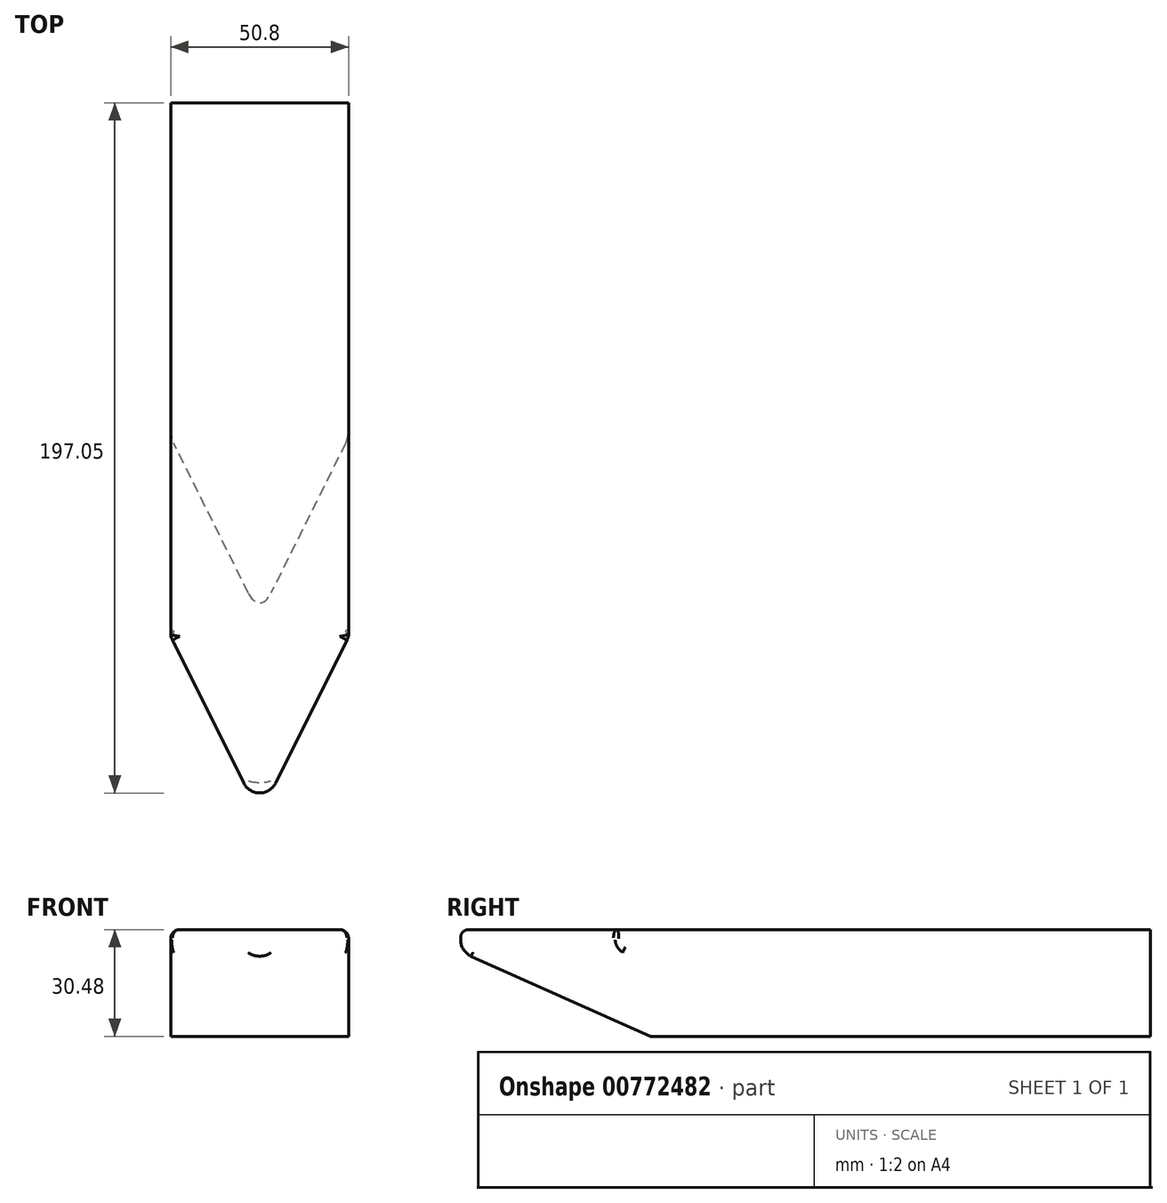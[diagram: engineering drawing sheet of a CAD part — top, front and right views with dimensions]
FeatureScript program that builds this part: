
annotation { "Feature Type Name" : "Feature", "Feature Type Description" : "" }
export const myFeature = defineFeature(function(context is Context, id is Id, definition is map)
    precondition{}
    {
        {
            var Q0;
            Q0=qCreatedBy(makeId("Top.planeOp"),FACE);
            var sketch = newSketch(context, id + "F0", { "sketchPlane" : qUnion([Q0])});
            skLineSegment(sketch, "E0.bottom", {"start": v(-25.4, 76.2) * mm, "end": v(25.4, 76.2) * mm});
            skLineSegment(sketch, "E0.top", {"start": v(-25.4, -76.2) * mm, "end": v(25.4, -76.2) * mm});
            skLineSegment(sketch, "E0.left", {"start": v(-25.4, 76.2) * mm, "end": v(-25.4, -76.2) * mm});
            skLineSegment(sketch, "E0.right", {"start": v(25.4, 76.2) * mm, "end": v(25.4, -76.2) * mm});
            skPoint(sketch, "E0.middle", {"position": v(0, 0) * mm});
            skLineSegment(sketch, "E1", {"start": v(-25.4, -76.2) * mm, "end": v(0, -127.15) * mm});
            skLineSegment(sketch, "E2", {"start": v(25.4, -76.2) * mm, "end": v(0, -127.15) * mm});
            skSolve(sketch);
        }
        {
            var Q0;
            Q0=makeQuery(id+"F0.imprint","IMPRINT",FACE,{"disambiguationData":[TD([[makeQuery(id+"F0.imprint","IMPRINT",EDGE,{"derivedFrom":sQuery(id+"F0.wireOp",EDGE,"E0.bottom")}),-1.0]])]});
            var Q1;
            Q1=makeQuery(id+"F0.imprint","IMPRINT",FACE,{"disambiguationData":[TD([[makeQuery(id+"F0.imprint","IMPRINT",EDGE,{"derivedFrom":sQuery(id+"F0.wireOp",EDGE,"E0.top")}),-1.0]])]});
            extrude(context, id + "F1", {"entities" : qUnion([Q0, Q1]), "depth" : 30.48 * mm, "offsetDistance" : 25.4 * mm});
        }
        {
            var Q0;
            Q0=makeQuery(id+"F1.opExtrude","CAP_EDGE",EDGE,{"disambiguationData":[OSD([sQuery(id+"F0.wireOp",EDGE,"E2")])],"isStart":true});
            var Q1;
            Q1=makeQuery(id+"F1.opExtrude","CAP_EDGE",EDGE,{"disambiguationData":[OSD([sQuery(id+"F0.wireOp",EDGE,"E1")])],"isStart":true});
            chamfer(context, id + "F2", {"entities" : qUnion([Q0, Q1]), "width" : 25.4 * mm, "tangentPropagation" : true});
        }
        {
            var Q0;
            {var subQ0=sQuery(id+"F0.wireOp",EDGE,"E2");Q0=makeQuery(id+"F2.opChamfer","BLEND_EDGE",EDGE,{"blendedFrom":[makeQuery(id+"F1.opExtrude","CAP_EDGE",EDGE,{"disambiguationData":[OSD([subQ0])],"isStart":true}),makeQuery(id+"F1.opExtrude","SWEPT_FACE",FACE,{"disambiguationData":[OSD([subQ0])]})],"blendedInto":[makeQuery(id+"F1.opExtrude","SWEPT_FACE",FACE,{"disambiguationData":[OSD([subQ0])]})]});}
            var Q1;
            {var subQ0=sQuery(id+"F0.wireOp",EDGE,"E1");Q1=makeQuery(id+"F2.opChamfer","BLEND_EDGE",EDGE,{"blendedFrom":[makeQuery(id+"F1.opExtrude","CAP_EDGE",EDGE,{"disambiguationData":[OSD([subQ0])],"isStart":true}),makeQuery(id+"F1.opExtrude","SWEPT_FACE",FACE,{"disambiguationData":[OSD([subQ0])]})],"blendedInto":[makeQuery(id+"F1.opExtrude","SWEPT_FACE",FACE,{"disambiguationData":[OSD([subQ0])]})]});}
            fillet(context, id + "F3", {"entities" : qUnion([Q0, Q1]), "radius" : 5.08 * mm, "tangentPropagation" : true, "allowEdgeOverflow" : false});
        }
        {
            var Q0;
            Q0=makeQuery(id+"F2.opChamfer","BLEND_EDGE",EDGE,{"blendedFrom":[makeQuery(id+"F1.opExtrude","CAP_EDGE",EDGE,{"disambiguationData":[OSD([sQuery(id+"F0.wireOp",EDGE,"E1")])],"isStart":true}),makeQuery(id+"F1.opExtrude","CAP_EDGE",EDGE,{"disambiguationData":[OSD([sQuery(id+"F0.wireOp",EDGE,"E2")])],"isStart":true})],"blendedInto":[]});
            fillet(context, id + "F4", {"entities" : qUnion([Q0]), "radius" : 5.08 * mm, "tangentPropagation" : true, "allowEdgeOverflow" : false});
        }
        {
            var Q0;
            Q0=makeQuery(id+"F1.opExtrude","CAP_EDGE",EDGE,{"disambiguationData":[OSD([sQuery(id+"F0.wireOp",EDGE,"E0.right")])],"isStart":false});
            var Q1;
            Q1=makeQuery(id+"F1.opExtrude","CAP_EDGE",EDGE,{"disambiguationData":[OSD([sQuery(id+"F0.wireOp",EDGE,"E0.left")])],"isStart":false});
            fillet(context, id + "F5", {"entities" : qUnion([Q0, Q1]), "radius" : 2.54 * mm, "tangentPropagation" : true, "allowEdgeOverflow" : false});
        }
        {
            var Q0;
            Q0=makeQuery(id+"F2.opChamfer","BLEND_EDGE",EDGE,{"blendedFrom":[makeQuery(id+"F1.opExtrude","CAP_EDGE",EDGE,{"disambiguationData":[OSD([sQuery(id+"F0.wireOp",EDGE,"E1")])],"isStart":true}),makeQuery(id+"F1.opExtrude","SWEPT_FACE",FACE,{"disambiguationData":[OSD([sQuery(id+"F0.wireOp",EDGE,"E0.left")])]})],"blendedInto":[makeQuery(id+"F1.opExtrude","SWEPT_FACE",FACE,{"disambiguationData":[OSD([sQuery(id+"F0.wireOp",EDGE,"E0.left")])]})]});
            var Q1;
            Q1=makeQuery(id+"F2.opChamfer","BLEND_EDGE",EDGE,{"blendedFrom":[makeQuery(id+"F1.opExtrude","CAP_EDGE",EDGE,{"disambiguationData":[OSD([sQuery(id+"F0.wireOp",EDGE,"E2")])],"isStart":true}),makeQuery(id+"F1.opExtrude","SWEPT_FACE",FACE,{"disambiguationData":[OSD([sQuery(id+"F0.wireOp",EDGE,"E0.right")])]})],"blendedInto":[makeQuery(id+"F1.opExtrude","SWEPT_FACE",FACE,{"disambiguationData":[OSD([sQuery(id+"F0.wireOp",EDGE,"E0.right")])]})]});
            fillet(context, id + "F6", {"entities" : qUnion([Q0, Q1]), "radius" : 2.3 * mm, "tangentPropagation" : true, "allowEdgeOverflow" : false});
        }
    });
